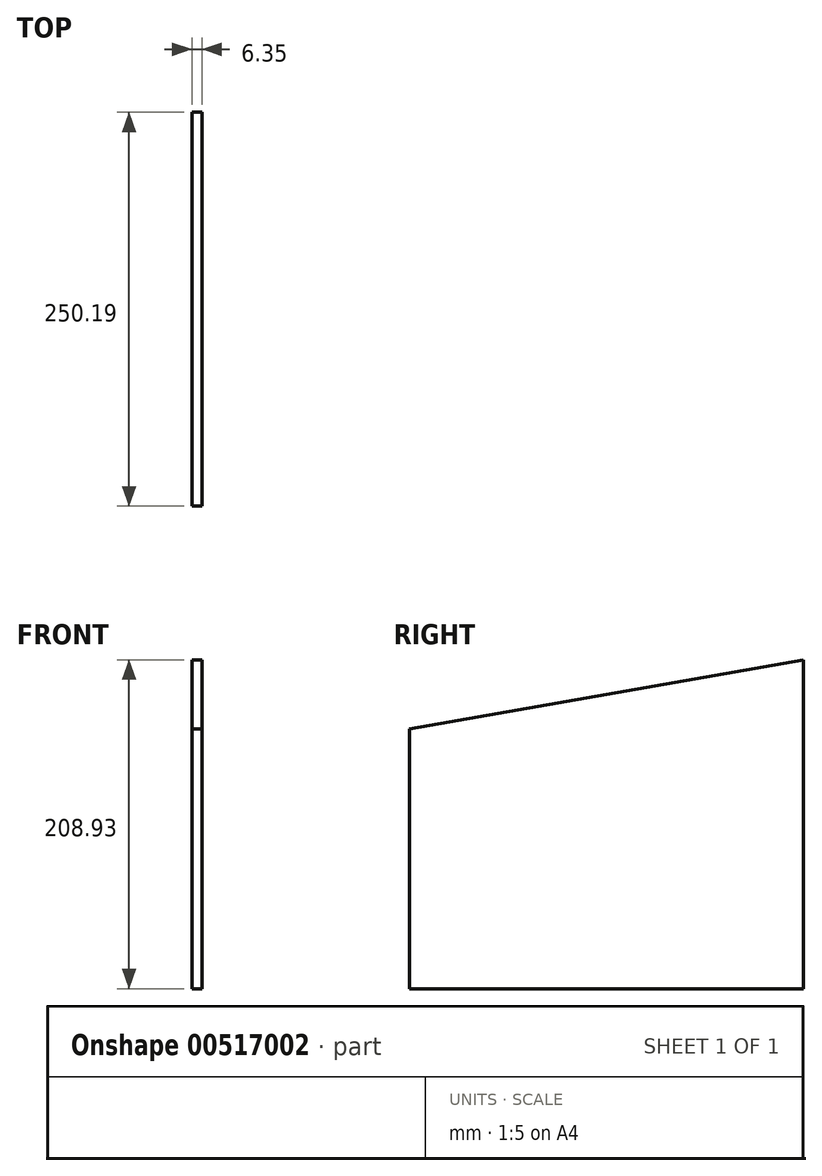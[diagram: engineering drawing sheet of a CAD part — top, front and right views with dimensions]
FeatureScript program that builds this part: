
annotation { "Feature Type Name" : "Feature", "Feature Type Description" : "" }
export const myFeature = defineFeature(function(context is Context, id is Id, definition is map)
    precondition{}
    {
        {
            var Q0;
            Q0=qCreatedBy(makeId("Right.planeOp"),FACE);
            var sketch = newSketch(context, id + "F0", { "sketchPlane" : qUnion([Q0])});
            skLineSegment(sketch, "E0.top", {"start": v(-218.74, -48.1) * mm, "end": v(31.45, -48.1) * mm});
            skLineSegment(sketch, "E0.left", {"start": v(-218.74, 117) * mm, "end": v(-218.74, -48.1) * mm});
            skLineSegment(sketch, "E0.right", {"start": v(31.45, 117) * mm, "end": v(31.45, -48.1) * mm});
            skLineSegment(sketch, "E1", {"start": v(-218.74, 117) * mm, "end": v(31.45, 160.83) * mm});
            skPoint(sketch, "E1.endSnap0", {"position": v(31.45, 34.45) * mm});
            skLineSegment(sketch, "E2", {"start": v(31.45, 160.83) * mm, "end": v(31.45, 117) * mm});
            skSolve(sketch);
        }
        {
            var Q0;
            Q0 = qSketchRegion(id + "F0", true);
            extrude(context, id + "F1", {"entities" : qUnion([Q0]), "depth" : 12.7 * mm, "offsetDistance" : 25.4 * mm});
        }
        {
            var Q0;
            Q0=makeQuery(id+"F1.opExtrude","CAP_FACE",FACE,{"disambiguationData":[OSD([sQuery(id+"F0.wireOp",EDGE,"E0.top"),sQuery(id+"F0.wireOp",EDGE,"E0.left"),sQuery(id+"F0.wireOp",EDGE,"E0.right"),sQuery(id+"F0.wireOp",EDGE,"E1"),sQuery(id+"F0.wireOp",EDGE,"E2")])],"isStart":false});
            extrude(context, id + "F2", {"entities" : qUnion([Q0]), "operationType" : NewBodyOperationType.REMOVE, "oppositeDirection" : true, "depth" : 6.35 * mm, "offsetDistance" : 25.4 * mm});
        }
    });
